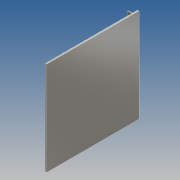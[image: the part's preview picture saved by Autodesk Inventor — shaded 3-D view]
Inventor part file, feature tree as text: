
AUTODESK INVENTOR PART (.ipt)
format: ipt  version: 2016 (Build 200138000, 138)  size: 154,112 bytes
history: native  units: mm
features: extrude x3, sketch x3, plane x1
ambient origin geometry x8: Origin, YZ Plane, XZ Plane, XY Plane, X Axis, Y Axis, Z Axis, Center Point
bodies: Solid1 (feature_tree)
feature tree (7):
  extrude  "Extrusion1"  Depth=2.0mm
  plane  "Work Plane1"
  extrude  "Extrusion2"  [1 undecoded]
  extrude  "Extrusion3"  Depth=1.0mm TaperAngle=0.0deg
  sketch  "Sketch1"  dims[d0=130.0mm d1=2.0mm]
  sketch  "Sketch2"  dims[d2=128.0mm d3=0.0mm d4=-8.0mm]
  sketch  "Sketch3"  dims[d5=6.0mm d6=1.0mm d7=0.0mm d8=0.5mm d9=5.0mm d10=120.0mm d12=10.0mm d13=10.0mm d15=10.0mm d17=0.5mm d18=0.0mm]
note: 1 required parameter value undecoded (feature->parameter linkage not recoverable at this tier; creation-order binding heuristic only, values carry confidence <= 0.55)
